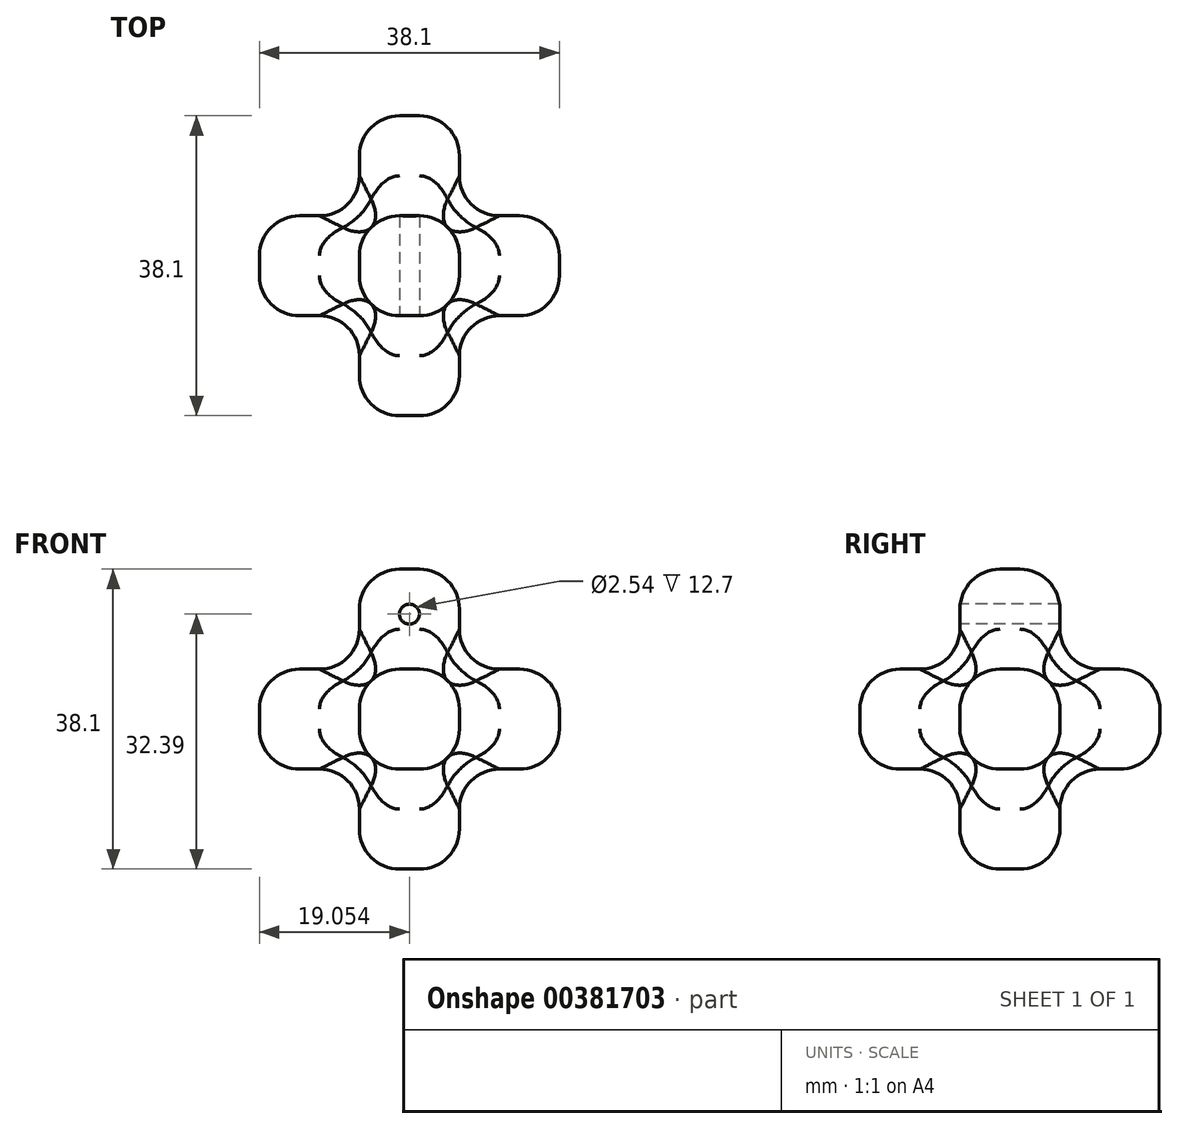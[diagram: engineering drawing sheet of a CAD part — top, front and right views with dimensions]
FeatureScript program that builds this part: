
annotation { "Feature Type Name" : "Feature", "Feature Type Description" : "" }
export const myFeature = defineFeature(function(context is Context, id is Id, definition is map)
    precondition{}
    {
        {
            var Q0;
            Q0=qCreatedBy(makeId("Front.planeOp"),FACE);
            var sketch = newSketch(context, id + "F0", { "sketchPlane" : qUnion([Q0])});
            skLineSegment(sketch, "E0", {"start": v(-30.28, 47.13) * mm, "end": v(-30.28, 34.43) * mm});
            skLineSegment(sketch, "E1", {"start": v(-30.28, 34.43) * mm, "end": v(-17.58, 34.43) * mm});
            skLineSegment(sketch, "E2", {"start": v(-17.58, 34.43) * mm, "end": v(-17.58, 21.73) * mm});
            skLineSegment(sketch, "E3", {"start": v(-17.58, 21.73) * mm, "end": v(-30.28, 21.73) * mm});
            skLineSegment(sketch, "E4", {"start": v(-30.28, 21.73) * mm, "end": v(-30.28, 9.03) * mm});
            skLineSegment(sketch, "E5", {"start": v(-30.28, 9.03) * mm, "end": v(-42.98, 9.03) * mm});
            skLineSegment(sketch, "E6", {"start": v(-42.98, 9.03) * mm, "end": v(-42.98, 21.73) * mm});
            skLineSegment(sketch, "E7", {"start": v(-42.98, 21.73) * mm, "end": v(-55.68, 21.73) * mm});
            skLineSegment(sketch, "E8", {"start": v(-55.68, 21.73) * mm, "end": v(-55.68, 34.43) * mm});
            skLineSegment(sketch, "E9", {"start": v(-55.68, 34.43) * mm, "end": v(-42.98, 34.43) * mm});
            skLineSegment(sketch, "E10", {"start": v(-42.98, 34.43) * mm, "end": v(-42.98, 47.13) * mm});
            skLineSegment(sketch, "E11", {"start": v(-42.98, 47.13) * mm, "end": v(-30.28, 47.13) * mm});
            skSolve(sketch);
        }
        {
            var Q0;
            Q0=makeQuery(id+"F0.imprint","IMPRINT",FACE,{"disambiguationData":[TD([[makeQuery(id+"F0.imprint","IMPRINT",EDGE,{"derivedFrom":sQuery(id+"F0.wireOp",EDGE,"E0")}),-1.0]])]});
            extrude(context, id + "F1", {"entities" : qUnion([Q0]), "depth" : 12.7 * mm});
        }
        {
            var Q0;
            Q0=makeQuery(id+"F1.opExtrude","CAP_FACE",FACE,{"disambiguationData":[OSD([sQuery(id+"F0.wireOp",EDGE,"E0"),sQuery(id+"F0.wireOp",EDGE,"E1"),sQuery(id+"F0.wireOp",EDGE,"E2"),sQuery(id+"F0.wireOp",EDGE,"E3"),sQuery(id+"F0.wireOp",EDGE,"E4"),sQuery(id+"F0.wireOp",EDGE,"E5"),sQuery(id+"F0.wireOp",EDGE,"E6"),sQuery(id+"F0.wireOp",EDGE,"E7"),sQuery(id+"F0.wireOp",EDGE,"E8"),sQuery(id+"F0.wireOp",EDGE,"E9"),sQuery(id+"F0.wireOp",EDGE,"E10"),sQuery(id+"F0.wireOp",EDGE,"E11")])],"isStart":false});
            var sketch = newSketch(context, id + "F2", { "sketchPlane" : qUnion([Q0])});
            skLineSegment(sketch, "E12", {"start": v(-42.98, 34.43) * mm, "end": v(-30.28, 34.43) * mm});
            skLineSegment(sketch, "E13", {"start": v(-30.28, 34.43) * mm, "end": v(-30.28, 21.73) * mm});
            skLineSegment(sketch, "E14", {"start": v(-30.28, 21.73) * mm, "end": v(-42.98, 21.73) * mm});
            skLineSegment(sketch, "E15", {"start": v(-42.98, 21.73) * mm, "end": v(-42.98, 34.43) * mm});
            skSolve(sketch);
        }
        {
            var Q0;
            Q0=makeQuery(id+"F2.imprint","IMPRINT",FACE,{"disambiguationData":[TD([[makeQuery(id+"F2.imprint","IMPRINT",EDGE,{"derivedFrom":sQuery(id+"F2.wireOp",EDGE,"E12")}),-1.0]])]});
            extrude(context, id + "F3", {"entities" : qUnion([Q0]), "operationType" : NewBodyOperationType.ADD, "depth" : 12.7 * mm});
        }
        {
            var Q0;
            Q0=makeQuery(id+"F1.opExtrude","CAP_FACE",FACE,{"disambiguationData":[OSD([sQuery(id+"F0.wireOp",EDGE,"E0"),sQuery(id+"F0.wireOp",EDGE,"E1"),sQuery(id+"F0.wireOp",EDGE,"E2"),sQuery(id+"F0.wireOp",EDGE,"E3"),sQuery(id+"F0.wireOp",EDGE,"E4"),sQuery(id+"F0.wireOp",EDGE,"E5"),sQuery(id+"F0.wireOp",EDGE,"E6"),sQuery(id+"F0.wireOp",EDGE,"E7"),sQuery(id+"F0.wireOp",EDGE,"E8"),sQuery(id+"F0.wireOp",EDGE,"E9"),sQuery(id+"F0.wireOp",EDGE,"E10"),sQuery(id+"F0.wireOp",EDGE,"E11")])],"isStart":true});
            var sketch = newSketch(context, id + "F4", { "sketchPlane" : qUnion([Q0])});
            skLineSegment(sketch, "E16", {"start": v(30.28, 34.43) * mm, "end": v(42.98, 34.43) * mm});
            skLineSegment(sketch, "E17", {"start": v(42.98, 34.43) * mm, "end": v(42.98, 21.73) * mm});
            skLineSegment(sketch, "E18", {"start": v(42.98, 21.73) * mm, "end": v(30.28, 21.73) * mm});
            skLineSegment(sketch, "E19", {"start": v(30.28, 21.73) * mm, "end": v(30.28, 34.43) * mm});
            skSolve(sketch);
        }
        {
            var Q0;
            Q0=qSketchRegion(id+"F4",true);
            extrude(context, id + "F5", {"entities" : qUnion([Q0]), "operationType" : NewBodyOperationType.ADD, "depth" : 12.7 * mm});
        }
        {
            var Q0;
            Q0=makeQuery(id+"F1.opExtrude","SWEPT_EDGE",EDGE,{"disambiguationData":[OSD([sQuery(id+"F0.wireOp",EDGE,"E10"),sQuery(id+"F0.wireOp",EDGE,"E11")])]});
            var Q1;
            Q1=makeQuery(id+"F1.opExtrude","CAP_EDGE",EDGE,{"disambiguationData":[OSD([sQuery(id+"F0.wireOp",EDGE,"E11")])],"isStart":false});
            var Q2;
            Q2=makeQuery(id+"F1.opExtrude","CAP_EDGE",EDGE,{"disambiguationData":[OSD([sQuery(id+"F0.wireOp",EDGE,"E11")])],"isStart":true});
            var Q3;
            Q3=makeQuery(id+"F1.opExtrude","SWEPT_EDGE",EDGE,{"disambiguationData":[OSD([sQuery(id+"F0.wireOp",EDGE,"E0"),sQuery(id+"F0.wireOp",EDGE,"E11")])]});
            var Q4;
            Q4=makeQuery(id+"F1.opExtrude","CAP_EDGE",EDGE,{"disambiguationData":[OSD([sQuery(id+"F0.wireOp",EDGE,"E10")])],"isStart":false});
            var Q5;
            Q5=makeQuery(id+"F1.opExtrude","CAP_EDGE",EDGE,{"disambiguationData":[OSD([sQuery(id+"F0.wireOp",EDGE,"E0")])],"isStart":false});
            var Q6;
            Q6=makeQuery(id+"F1.opExtrude","CAP_EDGE",EDGE,{"disambiguationData":[OSD([sQuery(id+"F0.wireOp",EDGE,"E0")])],"isStart":true});
            var Q7;
            Q7=makeQuery(id+"F1.opExtrude","CAP_EDGE",EDGE,{"disambiguationData":[OSD([sQuery(id+"F0.wireOp",EDGE,"E10")])],"isStart":true});
            fillet(context, id + "F6", {"entities" : qUnion([Q0, Q1, Q2, Q3, Q4, Q5, Q6, Q7]), "radius" : 5.08 * mm, "tangentPropagation" : true, "allowEdgeOverflow" : false});
        }
        {
            var Q0;
            Q0=makeQuery(id+"F3.opExtrude","SWEPT_EDGE",EDGE,{"disambiguationData":[OSD([sQuery(id+"F0.wireOp",EDGE,"E9"),sQuery(id+"F0.wireOp",EDGE,"E10"),sQuery(id+"F2.wireOp",EDGE,"E12"),sQuery(id+"F2.wireOp",EDGE,"E15")])]});
            var Q1;
            Q1=makeQuery(id+"F3.opExtrude","SWEPT_EDGE",EDGE,{"disambiguationData":[OSD([sQuery(id+"F0.wireOp",EDGE,"E0"),sQuery(id+"F0.wireOp",EDGE,"E1"),sQuery(id+"F2.wireOp",EDGE,"E12"),sQuery(id+"F2.wireOp",EDGE,"E13")])]});
            var Q2;
            Q2=makeQuery(id+"F3.opExtrude","SWEPT_EDGE",EDGE,{"disambiguationData":[OSD([sQuery(id+"F0.wireOp",EDGE,"E6"),sQuery(id+"F0.wireOp",EDGE,"E7"),sQuery(id+"F2.wireOp",EDGE,"E14"),sQuery(id+"F2.wireOp",EDGE,"E15")])]});
            var Q3;
            Q3=makeQuery(id+"F3.opExtrude","SWEPT_EDGE",EDGE,{"disambiguationData":[OSD([sQuery(id+"F0.wireOp",EDGE,"E3"),sQuery(id+"F0.wireOp",EDGE,"E4"),sQuery(id+"F2.wireOp",EDGE,"E13"),sQuery(id+"F2.wireOp",EDGE,"E14")])]});
            var Q4;
            Q4=makeQuery(id+"F3.opExtrude","CAP_EDGE",EDGE,{"disambiguationData":[OSD([sQuery(id+"F2.wireOp",EDGE,"E15")])],"isStart":false});
            var Q5;
            Q5=makeQuery(id+"F3.opExtrude","CAP_EDGE",EDGE,{"disambiguationData":[OSD([sQuery(id+"F2.wireOp",EDGE,"E12")])],"isStart":false});
            var Q6;
            Q6=makeQuery(id+"F3.opExtrude","CAP_EDGE",EDGE,{"disambiguationData":[OSD([sQuery(id+"F2.wireOp",EDGE,"E13")])],"isStart":false});
            var Q7;
            Q7=makeQuery(id+"F3.opExtrude","CAP_EDGE",EDGE,{"disambiguationData":[OSD([sQuery(id+"F2.wireOp",EDGE,"E14")])],"isStart":false});
            fillet(context, id + "F7", {"entities" : qUnion([Q0, Q1, Q2, Q3, Q4, Q5, Q6, Q7]), "radius" : 5.08 * mm, "tangentPropagation" : true, "allowEdgeOverflow" : false});
        }
        {
            var Q0;
            Q0=makeQuery(id+"F1.opExtrude","SWEPT_FACE",FACE,{"disambiguationData":[OSD([sQuery(id+"F0.wireOp",EDGE,"E8")])]});
            var Q1;
            Q1=makeQuery(id+"F1.opExtrude","CAP_EDGE",EDGE,{"disambiguationData":[OSD([sQuery(id+"F0.wireOp",EDGE,"E8")])],"isStart":false});
            var Q2;
            Q2=makeQuery(id+"F1.opExtrude","CAP_EDGE",EDGE,{"disambiguationData":[OSD([sQuery(id+"F0.wireOp",EDGE,"E8")])],"isStart":true});
            var Q3;
            Q3=makeQuery(id+"F1.opExtrude","CAP_EDGE",EDGE,{"disambiguationData":[OSD([sQuery(id+"F0.wireOp",EDGE,"E9")])],"isStart":true});
            var Q4;
            Q4=makeQuery(id+"F1.opExtrude","CAP_EDGE",EDGE,{"disambiguationData":[OSD([sQuery(id+"F0.wireOp",EDGE,"E7")])],"isStart":false});
            var Q5;
            Q5=makeQuery(id+"F1.opExtrude","CAP_EDGE",EDGE,{"disambiguationData":[OSD([sQuery(id+"F0.wireOp",EDGE,"E7")])],"isStart":true});
            var Q6;
            Q6=makeQuery(id+"F1.opExtrude","CAP_EDGE",EDGE,{"disambiguationData":[OSD([sQuery(id+"F0.wireOp",EDGE,"E9")])],"isStart":false});
            fillet(context, id + "F8", {"entities" : qUnion([Q0, Q1, Q2, Q3, Q4, Q5, Q6]), "radius" : 5.08 * mm, "tangentPropagation" : true, "allowEdgeOverflow" : false});
        }
        {
            var Q0;
            Q0=makeQuery(id+"F1.opExtrude","CAP_EDGE",EDGE,{"disambiguationData":[OSD([sQuery(id+"F0.wireOp",EDGE,"E1")])],"isStart":false});
            var Q1;
            Q1=makeQuery(id+"F1.opExtrude","CAP_EDGE",EDGE,{"disambiguationData":[OSD([sQuery(id+"F0.wireOp",EDGE,"E1")])],"isStart":true});
            var Q2;
            Q2=makeQuery(id+"F1.opExtrude","SWEPT_EDGE",EDGE,{"disambiguationData":[OSD([sQuery(id+"F0.wireOp",EDGE,"E1"),sQuery(id+"F0.wireOp",EDGE,"E2")])]});
            var Q3;
            Q3=makeQuery(id+"F1.opExtrude","CAP_EDGE",EDGE,{"disambiguationData":[OSD([sQuery(id+"F0.wireOp",EDGE,"E2")])],"isStart":true});
            var Q4;
            Q4=makeQuery(id+"F1.opExtrude","SWEPT_EDGE",EDGE,{"disambiguationData":[OSD([sQuery(id+"F0.wireOp",EDGE,"E2"),sQuery(id+"F0.wireOp",EDGE,"E3")])]});
            var Q5;
            Q5=makeQuery(id+"F1.opExtrude","CAP_EDGE",EDGE,{"disambiguationData":[OSD([sQuery(id+"F0.wireOp",EDGE,"E2")])],"isStart":false});
            var Q6;
            Q6=makeQuery(id+"F1.opExtrude","CAP_EDGE",EDGE,{"disambiguationData":[OSD([sQuery(id+"F0.wireOp",EDGE,"E3")])],"isStart":false});
            var Q7;
            Q7=makeQuery(id+"F1.opExtrude","CAP_EDGE",EDGE,{"disambiguationData":[OSD([sQuery(id+"F0.wireOp",EDGE,"E3")])],"isStart":true});
            fillet(context, id + "F9", {"entities" : qUnion([Q0, Q1, Q2, Q3, Q4, Q5, Q6, Q7]), "radius" : 5.08 * mm, "tangentPropagation" : true, "allowEdgeOverflow" : false});
        }
        {
            var Q0;
            Q0=makeQuery(id+"F1.opExtrude","CAP_EDGE",EDGE,{"disambiguationData":[OSD([sQuery(id+"F0.wireOp",EDGE,"E6")])],"isStart":true});
            var Q1;
            Q1=makeQuery(id+"F1.opExtrude","CAP_EDGE",EDGE,{"disambiguationData":[OSD([sQuery(id+"F0.wireOp",EDGE,"E6")])],"isStart":false});
            var Q2;
            Q2=makeQuery(id+"F1.opExtrude","CAP_EDGE",EDGE,{"disambiguationData":[OSD([sQuery(id+"F0.wireOp",EDGE,"E4")])],"isStart":false});
            var Q3;
            Q3=makeQuery(id+"F1.opExtrude","CAP_EDGE",EDGE,{"disambiguationData":[OSD([sQuery(id+"F0.wireOp",EDGE,"E4")])],"isStart":true});
            var Q4;
            Q4=makeQuery(id+"F1.opExtrude","SWEPT_EDGE",EDGE,{"disambiguationData":[OSD([sQuery(id+"F0.wireOp",EDGE,"E4"),sQuery(id+"F0.wireOp",EDGE,"E5")])]});
            var Q5;
            Q5=makeQuery(id+"F1.opExtrude","CAP_EDGE",EDGE,{"disambiguationData":[OSD([sQuery(id+"F0.wireOp",EDGE,"E5")])],"isStart":false});
            var Q6;
            Q6=makeQuery(id+"F1.opExtrude","SWEPT_EDGE",EDGE,{"disambiguationData":[OSD([sQuery(id+"F0.wireOp",EDGE,"E5"),sQuery(id+"F0.wireOp",EDGE,"E6")])]});
            var Q7;
            Q7=makeQuery(id+"F1.opExtrude","CAP_EDGE",EDGE,{"disambiguationData":[OSD([sQuery(id+"F0.wireOp",EDGE,"E5")])],"isStart":true});
            fillet(context, id + "F10", {"entities" : qUnion([Q0, Q1, Q2, Q3, Q4, Q5, Q6, Q7]), "radius" : 5.08 * mm, "tangentPropagation" : true, "allowEdgeOverflow" : false});
        }
        {
            var Q0;
            Q0=makeQuery(id+"F5.opExtrude","SWEPT_EDGE",EDGE,{"disambiguationData":[OSD([sQuery(id+"F0.wireOp",EDGE,"E3"),sQuery(id+"F0.wireOp",EDGE,"E4"),sQuery(id+"F4.wireOp",EDGE,"E18"),sQuery(id+"F4.wireOp",EDGE,"E19")])]});
            fillet(context, id + "F11", {"entities" : qUnion([Q0]), "radius" : 5.08 * mm, "tangentPropagation" : true, "allowEdgeOverflow" : false});
        }
        {
            var Q0;
            Q0=makeQuery(id+"F5.opExtrude","SWEPT_EDGE",EDGE,{"disambiguationData":[OSD([sQuery(id+"F0.wireOp",EDGE,"E0"),sQuery(id+"F0.wireOp",EDGE,"E1"),sQuery(id+"F4.wireOp",EDGE,"E16"),sQuery(id+"F4.wireOp",EDGE,"E19")])]});
            var Q1;
            Q1=makeQuery(id+"F5.opExtrude","SWEPT_EDGE",EDGE,{"disambiguationData":[OSD([sQuery(id+"F0.wireOp",EDGE,"E9"),sQuery(id+"F0.wireOp",EDGE,"E10"),sQuery(id+"F4.wireOp",EDGE,"E16"),sQuery(id+"F4.wireOp",EDGE,"E17")])]});
            var Q2;
            Q2=makeQuery(id+"F5.opExtrude","SWEPT_EDGE",EDGE,{"disambiguationData":[OSD([sQuery(id+"F0.wireOp",EDGE,"E6"),sQuery(id+"F0.wireOp",EDGE,"E7"),sQuery(id+"F4.wireOp",EDGE,"E17"),sQuery(id+"F4.wireOp",EDGE,"E18")])]});
            fillet(context, id + "F12", {"entities" : qUnion([Q0, Q1, Q2]), "radius" : 5.08 * mm, "tangentPropagation" : true, "allowEdgeOverflow" : false});
        }
        {
            var Q0;
            Q0=makeQuery(id+"F5.opExtrude","CAP_FACE",FACE,{"disambiguationData":[OSD([sQuery(id+"F4.wireOp",EDGE,"E16"),sQuery(id+"F4.wireOp",EDGE,"E17"),sQuery(id+"F4.wireOp",EDGE,"E18"),sQuery(id+"F4.wireOp",EDGE,"E19")])],"isStart":false});
            var Q1;
            {var subQ0=sQuery(id+"F0.wireOp",EDGE,"E9");var subQ1=makeQuery(id+"F1.opExtrude","SWEPT_FACE",FACE,{"disambiguationData":[OSD([subQ0])]});var subQ2=sQuery(id+"F0.wireOp",EDGE,"E0");var subQ4=sQuery(id+"F0.wireOp",EDGE,"E1");var subQ5=makeQuery(id+"F1.opExtrude","SWEPT_FACE",FACE,{"disambiguationData":[OSD([subQ4])]});var subQ6=sQuery(id+"F0.wireOp",EDGE,"E11");var subQ7=sQuery(id+"F0.wireOp",EDGE,"E10");var subQ8=sQuery(id+"F0.wireOp",EDGE,"E8");var subQ9=sQuery(id+"F0.wireOp",EDGE,"E7");var subQ10=sQuery(id+"F0.wireOp",EDGE,"E6");var subQ11=sQuery(id+"F0.wireOp",EDGE,"E5");var subQ12=sQuery(id+"F0.wireOp",EDGE,"E4");var subQ13=sQuery(id+"F0.wireOp",EDGE,"E3");var subQ14=sQuery(id+"F0.wireOp",EDGE,"E2");var subQ15=makeQuery(id+"F1.opExtrude","CAP_FACE",FACE,{"disambiguationData":[OSD([subQ2,subQ4,subQ14,subQ13,subQ12,subQ11,subQ10,subQ9,subQ8,subQ0,subQ7,subQ6])],"isStart":false});var subQ17=sQuery(id+"F2.wireOp",EDGE,"E12");var subQ18=makeQuery(id+"F3.opExtrude","SWEPT_FACE",FACE,{"disambiguationData":[OSD([subQ17])]});var subQ19=sQuery(id+"F2.wireOp",EDGE,"E13");Q1=makeQuery(id+"F9.opFillet","TWEAK_EDGE",EDGE,{"derivedFrom":[makeQuery(id+"F7.opFillet","BLEND_VERTEX",VERTEX,{"blendedFrom":[makeQuery(id+"F3.opExtrude","SWEPT_EDGE",EDGE,{"disambiguationData":[OSD([subQ2,subQ4,subQ17,subQ19])]}),makeQuery(id+"F3.boolean.opBoolean","SPLIT",FACE,{"disambiguationData":[TD([makeQuery(id+"F1.opExtrude","SWEPT_FACE",FACE,{"disambiguationData":[OSD([subQ14])]})])],"derivedFrom":subQ15}),makeQuery(id+"F3.boolean.opBoolean","SPLIT",FACE,{"disambiguationData":[TD([makeQuery(id+"F1.opExtrude","SWEPT_FACE",FACE,{"disambiguationData":[OSD([subQ11])]})])],"derivedFrom":subQ15}),makeQuery(id+"F3.boolean.opBoolean","SPLIT",FACE,{"disambiguationData":[TD([makeQuery(id+"F1.opExtrude","SWEPT_FACE",FACE,{"disambiguationData":[OSD([subQ8])]})])],"derivedFrom":subQ15}),makeQuery(id+"F6.opFillet","BLEND_FACE",FACE,{"disambiguationData":[OSD([subQ2]),TDD([makeQuery(id+"F1.opExtrude","CAP_EDGE",EDGE,{"disambiguationData":[OSD([subQ2])],"isStart":false})])]}),makeQuery(id+"F6.opFillet","MERGE",FACE,{"derivedFrom":[subQ5,subQ1,subQ18,makeQuery(id+"F5.opExtrude","SWEPT_FACE",FACE,{"disambiguationData":[OSD([sQuery(id+"F4.wireOp",EDGE,"E16")])]})]}),makeQuery(id+"F3.boolean.opBoolean","SPLIT",FACE,{"disambiguationData":[TD([makeQuery(id+"F1.opExtrude","SWEPT_FACE",FACE,{"disambiguationData":[OSD([subQ6])]})])],"derivedFrom":subQ15})],"blendedInto":[makeQuery(id+"F3.boolean.opBoolean","SPLIT",FACE,{"disambiguationData":[TD([makeQuery(id+"F1.opExtrude","SWEPT_FACE",FACE,{"disambiguationData":[OSD([subQ14])]})])],"derivedFrom":subQ15}),makeQuery(id+"F3.boolean.opBoolean","SPLIT",FACE,{"disambiguationData":[TD([makeQuery(id+"F1.opExtrude","SWEPT_FACE",FACE,{"disambiguationData":[OSD([subQ11])]})])],"derivedFrom":subQ15}),makeQuery(id+"F3.boolean.opBoolean","SPLIT",FACE,{"disambiguationData":[TD([makeQuery(id+"F1.opExtrude","SWEPT_FACE",FACE,{"disambiguationData":[OSD([subQ8])]})])],"derivedFrom":subQ15}),makeQuery(id+"F6.opFillet","BLEND_FACE",FACE,{"disambiguationData":[OSD([subQ2]),TDD([makeQuery(id+"F1.opExtrude","CAP_EDGE",EDGE,{"disambiguationData":[OSD([subQ2])],"isStart":false})])]}),makeQuery(id+"F6.opFillet","MERGE",FACE,{"derivedFrom":[subQ5,subQ1,subQ18,makeQuery(id+"F5.opExtrude","SWEPT_FACE",FACE,{"disambiguationData":[OSD([sQuery(id+"F4.wireOp",EDGE,"E16")])]})]}),makeQuery(id+"F3.boolean.opBoolean","SPLIT",FACE,{"disambiguationData":[TD([makeQuery(id+"F1.opExtrude","SWEPT_FACE",FACE,{"disambiguationData":[OSD([subQ6])]})])],"derivedFrom":subQ15})]})]});}
            var Q2;
            {var subQ0=sQuery(id+"F0.wireOp",EDGE,"E10");Q2=makeQuery(id+"F8.opFillet","BLEND_EDGE",EDGE,{"blendedFrom":[makeQuery(id+"F1.opExtrude","CAP_EDGE",EDGE,{"disambiguationData":[OSD([sQuery(id+"F0.wireOp",EDGE,"E9")])],"isStart":false}),makeQuery(id+"F6.opFillet","BLEND_FACE",FACE,{"disambiguationData":[OSD([subQ0]),TDD([makeQuery(id+"F1.opExtrude","CAP_EDGE",EDGE,{"disambiguationData":[OSD([subQ0])],"isStart":false})])]})],"blendedInto":[makeQuery(id+"F6.opFillet","BLEND_FACE",FACE,{"disambiguationData":[OSD([subQ0]),TDD([makeQuery(id+"F1.opExtrude","CAP_EDGE",EDGE,{"disambiguationData":[OSD([subQ0])],"isStart":false})])]})]});}
            var Q3;
            {var subQ0=sQuery(id+"F0.wireOp",EDGE,"E9");var subQ1=makeQuery(id+"F1.opExtrude","SWEPT_FACE",FACE,{"disambiguationData":[OSD([subQ0])]});var subQ2=sQuery(id+"F0.wireOp",EDGE,"E0");var subQ4=sQuery(id+"F0.wireOp",EDGE,"E1");var subQ5=makeQuery(id+"F1.opExtrude","SWEPT_FACE",FACE,{"disambiguationData":[OSD([subQ4])]});var subQ6=sQuery(id+"F0.wireOp",EDGE,"E11");var subQ7=sQuery(id+"F0.wireOp",EDGE,"E10");var subQ8=sQuery(id+"F0.wireOp",EDGE,"E8");var subQ9=sQuery(id+"F0.wireOp",EDGE,"E7");var subQ10=sQuery(id+"F0.wireOp",EDGE,"E6");var subQ11=sQuery(id+"F0.wireOp",EDGE,"E5");var subQ12=sQuery(id+"F0.wireOp",EDGE,"E4");var subQ13=sQuery(id+"F0.wireOp",EDGE,"E3");var subQ14=sQuery(id+"F0.wireOp",EDGE,"E2");var subQ15=makeQuery(id+"F1.opExtrude","CAP_FACE",FACE,{"disambiguationData":[OSD([subQ2,subQ4,subQ14,subQ13,subQ12,subQ11,subQ10,subQ9,subQ8,subQ0,subQ7,subQ6])],"isStart":false});var subQ17=sQuery(id+"F2.wireOp",EDGE,"E12");var subQ18=makeQuery(id+"F3.opExtrude","SWEPT_FACE",FACE,{"disambiguationData":[OSD([subQ17])]});var subQ20=sQuery(id+"F2.wireOp",EDGE,"E15");Q3=makeQuery(id+"F8.opFillet","TWEAK_EDGE",EDGE,{"derivedFrom":[makeQuery(id+"F7.opFillet","BLEND_VERTEX",VERTEX,{"blendedFrom":[makeQuery(id+"F3.opExtrude","SWEPT_EDGE",EDGE,{"disambiguationData":[OSD([subQ0,subQ7,subQ17,subQ20])]}),makeQuery(id+"F3.boolean.opBoolean","SPLIT",FACE,{"disambiguationData":[TD([makeQuery(id+"F1.opExtrude","SWEPT_FACE",FACE,{"disambiguationData":[OSD([subQ14])]})])],"derivedFrom":subQ15}),makeQuery(id+"F3.boolean.opBoolean","SPLIT",FACE,{"disambiguationData":[TD([makeQuery(id+"F1.opExtrude","SWEPT_FACE",FACE,{"disambiguationData":[OSD([subQ11])]})])],"derivedFrom":subQ15}),makeQuery(id+"F3.boolean.opBoolean","SPLIT",FACE,{"disambiguationData":[TD([makeQuery(id+"F1.opExtrude","SWEPT_FACE",FACE,{"disambiguationData":[OSD([subQ8])]})])],"derivedFrom":subQ15}),makeQuery(id+"F6.opFillet","BLEND_FACE",FACE,{"disambiguationData":[OSD([subQ7]),TDD([makeQuery(id+"F1.opExtrude","CAP_EDGE",EDGE,{"disambiguationData":[OSD([subQ7])],"isStart":false})])]}),makeQuery(id+"F6.opFillet","MERGE",FACE,{"derivedFrom":[subQ5,subQ1,subQ18,makeQuery(id+"F5.opExtrude","SWEPT_FACE",FACE,{"disambiguationData":[OSD([sQuery(id+"F4.wireOp",EDGE,"E16")])]})]}),makeQuery(id+"F3.boolean.opBoolean","SPLIT",FACE,{"disambiguationData":[TD([makeQuery(id+"F1.opExtrude","SWEPT_FACE",FACE,{"disambiguationData":[OSD([subQ6])]})])],"derivedFrom":subQ15})],"blendedInto":[makeQuery(id+"F3.boolean.opBoolean","SPLIT",FACE,{"disambiguationData":[TD([makeQuery(id+"F1.opExtrude","SWEPT_FACE",FACE,{"disambiguationData":[OSD([subQ14])]})])],"derivedFrom":subQ15}),makeQuery(id+"F3.boolean.opBoolean","SPLIT",FACE,{"disambiguationData":[TD([makeQuery(id+"F1.opExtrude","SWEPT_FACE",FACE,{"disambiguationData":[OSD([subQ11])]})])],"derivedFrom":subQ15}),makeQuery(id+"F3.boolean.opBoolean","SPLIT",FACE,{"disambiguationData":[TD([makeQuery(id+"F1.opExtrude","SWEPT_FACE",FACE,{"disambiguationData":[OSD([subQ8])]})])],"derivedFrom":subQ15}),makeQuery(id+"F6.opFillet","BLEND_FACE",FACE,{"disambiguationData":[OSD([subQ7]),TDD([makeQuery(id+"F1.opExtrude","CAP_EDGE",EDGE,{"disambiguationData":[OSD([subQ7])],"isStart":false})])]}),makeQuery(id+"F6.opFillet","MERGE",FACE,{"derivedFrom":[subQ5,subQ1,subQ18,makeQuery(id+"F5.opExtrude","SWEPT_FACE",FACE,{"disambiguationData":[OSD([sQuery(id+"F4.wireOp",EDGE,"E16")])]})]}),makeQuery(id+"F3.boolean.opBoolean","SPLIT",FACE,{"disambiguationData":[TD([makeQuery(id+"F1.opExtrude","SWEPT_FACE",FACE,{"disambiguationData":[OSD([subQ6])]})])],"derivedFrom":subQ15})]})]});}
            var Q4;
            {var subQ0=sQuery(id+"F2.wireOp",EDGE,"E15");var subQ1=sQuery(id+"F2.wireOp",EDGE,"E12");var subQ2=sQuery(id+"F0.wireOp",EDGE,"E10");var subQ3=sQuery(id+"F0.wireOp",EDGE,"E9");Q4=makeQuery(id+"F8.opFillet","BLEND_EDGE",EDGE,{"blendedFrom":[makeQuery(id+"F1.opExtrude","CAP_EDGE",EDGE,{"disambiguationData":[OSD([subQ3])],"isStart":false}),makeQuery(id+"F7.opFillet","BLEND_FACE",FACE,{"disambiguationData":[OSD([subQ3,subQ2,subQ1,subQ0]),TDD([makeQuery(id+"F3.opExtrude","SWEPT_EDGE",EDGE,{"disambiguationData":[OSD([subQ3,subQ2,subQ1,subQ0])]})])]})],"blendedInto":[makeQuery(id+"F7.opFillet","BLEND_FACE",FACE,{"disambiguationData":[OSD([subQ3,subQ2,subQ1,subQ0]),TDD([makeQuery(id+"F3.opExtrude","SWEPT_EDGE",EDGE,{"disambiguationData":[OSD([subQ3,subQ2,subQ1,subQ0])]})])]})]});}
            var Q5;
            Q5=makeQuery(id+"F3.opExtrude","CAP_EDGE",EDGE,{"disambiguationData":[OSD([sQuery(id+"F2.wireOp",EDGE,"E12")])],"isStart":true});
            var Q6;
            {var subQ0=sQuery(id+"F0.wireOp",EDGE,"E7");Q6=makeQuery(id+"F10.opFillet","BLEND_EDGE",EDGE,{"blendedFrom":[makeQuery(id+"F1.opExtrude","CAP_EDGE",EDGE,{"disambiguationData":[OSD([sQuery(id+"F0.wireOp",EDGE,"E6")])],"isStart":false}),makeQuery(id+"F8.opFillet","BLEND_FACE",FACE,{"disambiguationData":[OSD([subQ0]),TDD([makeQuery(id+"F1.opExtrude","CAP_EDGE",EDGE,{"disambiguationData":[OSD([subQ0])],"isStart":false})])]})],"blendedInto":[makeQuery(id+"F8.opFillet","BLEND_FACE",FACE,{"disambiguationData":[OSD([subQ0]),TDD([makeQuery(id+"F1.opExtrude","CAP_EDGE",EDGE,{"disambiguationData":[OSD([subQ0])],"isStart":false})])]})]});}
            var Q7;
            {var subQ0=sQuery(id+"F2.wireOp",EDGE,"E15");var subQ1=sQuery(id+"F2.wireOp",EDGE,"E14");var subQ2=sQuery(id+"F0.wireOp",EDGE,"E7");var subQ3=sQuery(id+"F0.wireOp",EDGE,"E6");Q7=makeQuery(id+"F10.opFillet","BLEND_EDGE",EDGE,{"blendedFrom":[makeQuery(id+"F1.opExtrude","CAP_EDGE",EDGE,{"disambiguationData":[OSD([subQ3])],"isStart":false}),makeQuery(id+"F7.opFillet","BLEND_FACE",FACE,{"disambiguationData":[OSD([subQ3,subQ2,subQ1,subQ0]),TDD([makeQuery(id+"F3.opExtrude","SWEPT_EDGE",EDGE,{"disambiguationData":[OSD([subQ3,subQ2,subQ1,subQ0])]})])]})],"blendedInto":[makeQuery(id+"F7.opFillet","BLEND_FACE",FACE,{"disambiguationData":[OSD([subQ3,subQ2,subQ1,subQ0]),TDD([makeQuery(id+"F3.opExtrude","SWEPT_EDGE",EDGE,{"disambiguationData":[OSD([subQ3,subQ2,subQ1,subQ0])]})])]})]});}
            var Q8;
            {var subQ0=sQuery(id+"F2.wireOp",EDGE,"E15");var subQ1=makeQuery(id+"F3.opExtrude","SWEPT_FACE",FACE,{"disambiguationData":[OSD([subQ0])]});var subQ2=sQuery(id+"F0.wireOp",EDGE,"E8");var subQ3=sQuery(id+"F0.wireOp",EDGE,"E7");var subQ5=sQuery(id+"F0.wireOp",EDGE,"E6");var subQ6=makeQuery(id+"F1.opExtrude","SWEPT_FACE",FACE,{"disambiguationData":[OSD([subQ5])]});var subQ7=sQuery(id+"F0.wireOp",EDGE,"E10");var subQ8=sQuery(id+"F0.wireOp",EDGE,"E9");var subQ9=sQuery(id+"F0.wireOp",EDGE,"E5");var subQ10=sQuery(id+"F0.wireOp",EDGE,"E4");var subQ11=sQuery(id+"F0.wireOp",EDGE,"E3");var subQ12=sQuery(id+"F0.wireOp",EDGE,"E2");var subQ13=sQuery(id+"F0.wireOp",EDGE,"E1");var subQ14=sQuery(id+"F0.wireOp",EDGE,"E0");var subQ15=makeQuery(id+"F1.opExtrude","CAP_FACE",FACE,{"disambiguationData":[OSD([subQ14,subQ13,subQ12,subQ11,subQ10,subQ9,subQ5,subQ3,subQ2,subQ8,subQ7,sQuery(id+"F0.wireOp",EDGE,"E11")])],"isStart":false});var subQ17=sQuery(id+"F2.wireOp",EDGE,"E14");Q8=makeQuery(id+"F10.opFillet","TWEAK_EDGE",EDGE,{"derivedFrom":[makeQuery(id+"F8.opFillet","BLEND_VERTEX",VERTEX,{"blendedFrom":[makeQuery(id+"F1.opExtrude","CAP_EDGE",EDGE,{"disambiguationData":[OSD([subQ3])],"isStart":false}),subQ6,makeQuery(id+"F5.opExtrude","SWEPT_FACE",FACE,{"disambiguationData":[OSD([sQuery(id+"F4.wireOp",EDGE,"E17")])]}),makeQuery(id+"F7.opFillet","BLEND_FACE",FACE,{"disambiguationData":[OSD([subQ5,subQ3,subQ17,subQ0]),TDD([makeQuery(id+"F3.opExtrude","SWEPT_EDGE",EDGE,{"disambiguationData":[OSD([subQ5,subQ3,subQ17,subQ0])]})])]}),makeQuery(id+"F7.opFillet","MERGE",FACE,{"derivedFrom":[makeQuery(id+"F3.boolean.opBoolean","SPLIT",FACE,{"disambiguationData":[TD([makeQuery(id+"F1.opExtrude","SWEPT_FACE",FACE,{"disambiguationData":[OSD([subQ12])]})])],"derivedFrom":subQ15}),makeQuery(id+"F3.boolean.opBoolean","SPLIT",FACE,{"disambiguationData":[TD([makeQuery(id+"F1.opExtrude","SWEPT_FACE",FACE,{"disambiguationData":[OSD([subQ9])]})])],"derivedFrom":subQ15}),makeQuery(id+"F3.boolean.opBoolean","SPLIT",FACE,{"disambiguationData":[TD([makeQuery(id+"F1.opExtrude","SWEPT_FACE",FACE,{"disambiguationData":[OSD([subQ2])]})])],"derivedFrom":subQ15})]}),subQ1],"blendedInto":[subQ6,makeQuery(id+"F5.opExtrude","SWEPT_FACE",FACE,{"disambiguationData":[OSD([sQuery(id+"F4.wireOp",EDGE,"E17")])]}),makeQuery(id+"F7.opFillet","BLEND_FACE",FACE,{"disambiguationData":[OSD([subQ5,subQ3,subQ17,subQ0]),TDD([makeQuery(id+"F3.opExtrude","SWEPT_EDGE",EDGE,{"disambiguationData":[OSD([subQ5,subQ3,subQ17,subQ0])]})])]}),makeQuery(id+"F7.opFillet","MERGE",FACE,{"derivedFrom":[makeQuery(id+"F3.boolean.opBoolean","SPLIT",FACE,{"disambiguationData":[TD([makeQuery(id+"F1.opExtrude","SWEPT_FACE",FACE,{"disambiguationData":[OSD([subQ12])]})])],"derivedFrom":subQ15}),makeQuery(id+"F3.boolean.opBoolean","SPLIT",FACE,{"disambiguationData":[TD([makeQuery(id+"F1.opExtrude","SWEPT_FACE",FACE,{"disambiguationData":[OSD([subQ9])]})])],"derivedFrom":subQ15}),makeQuery(id+"F3.boolean.opBoolean","SPLIT",FACE,{"disambiguationData":[TD([makeQuery(id+"F1.opExtrude","SWEPT_FACE",FACE,{"disambiguationData":[OSD([subQ2])]})])],"derivedFrom":subQ15})]}),subQ1]})]});}
            var Q9;
            Q9=makeQuery(id+"F3.opExtrude","CAP_EDGE",EDGE,{"disambiguationData":[OSD([sQuery(id+"F2.wireOp",EDGE,"E15")])],"isStart":true});
            var Q10;
            {var subQ0=sQuery(id+"F2.wireOp",EDGE,"E14");var subQ1=sQuery(id+"F2.wireOp",EDGE,"E13");var subQ2=sQuery(id+"F0.wireOp",EDGE,"E4");var subQ3=sQuery(id+"F0.wireOp",EDGE,"E3");Q10=makeQuery(id+"F10.opFillet","BLEND_EDGE",EDGE,{"blendedFrom":[makeQuery(id+"F1.opExtrude","CAP_EDGE",EDGE,{"disambiguationData":[OSD([subQ2])],"isStart":false}),makeQuery(id+"F7.opFillet","BLEND_FACE",FACE,{"disambiguationData":[OSD([subQ3,subQ2,subQ1,subQ0]),TDD([makeQuery(id+"F3.opExtrude","SWEPT_EDGE",EDGE,{"disambiguationData":[OSD([subQ3,subQ2,subQ1,subQ0])]})])]})],"blendedInto":[makeQuery(id+"F7.opFillet","BLEND_FACE",FACE,{"disambiguationData":[OSD([subQ3,subQ2,subQ1,subQ0]),TDD([makeQuery(id+"F3.opExtrude","SWEPT_EDGE",EDGE,{"disambiguationData":[OSD([subQ3,subQ2,subQ1,subQ0])]})])]})]});}
            var Q11;
            Q11=makeQuery(id+"F3.opExtrude","CAP_EDGE",EDGE,{"disambiguationData":[OSD([sQuery(id+"F2.wireOp",EDGE,"E14")])],"isStart":true});
            var Q12;
            {var subQ0=sQuery(id+"F0.wireOp",EDGE,"E8");var subQ1=sQuery(id+"F0.wireOp",EDGE,"E7");var subQ3=sQuery(id+"F0.wireOp",EDGE,"E6");var subQ5=sQuery(id+"F0.wireOp",EDGE,"E10");var subQ6=sQuery(id+"F0.wireOp",EDGE,"E9");var subQ7=sQuery(id+"F0.wireOp",EDGE,"E5");var subQ8=sQuery(id+"F0.wireOp",EDGE,"E4");var subQ9=sQuery(id+"F0.wireOp",EDGE,"E3");var subQ10=sQuery(id+"F0.wireOp",EDGE,"E2");var subQ11=sQuery(id+"F0.wireOp",EDGE,"E1");var subQ12=sQuery(id+"F0.wireOp",EDGE,"E0");var subQ13=makeQuery(id+"F1.opExtrude","CAP_FACE",FACE,{"disambiguationData":[OSD([subQ12,subQ11,subQ10,subQ9,subQ8,subQ7,subQ3,subQ1,subQ0,subQ6,subQ5,sQuery(id+"F0.wireOp",EDGE,"E11")])],"isStart":false});var subQ15=sQuery(id+"F2.wireOp",EDGE,"E14");var subQ18=makeQuery(id+"F1.opExtrude","SWEPT_FACE",FACE,{"disambiguationData":[OSD([subQ8])]});var subQ20=sQuery(id+"F2.wireOp",EDGE,"E13");var subQ21=makeQuery(id+"F3.opExtrude","SWEPT_FACE",FACE,{"disambiguationData":[OSD([subQ20])]});Q12=makeQuery(id+"F10.opFillet","TWEAK_EDGE",EDGE,{"derivedFrom":[makeQuery(id+"F9.opFillet","BLEND_VERTEX",VERTEX,{"blendedFrom":[makeQuery(id+"F1.opExtrude","CAP_EDGE",EDGE,{"disambiguationData":[OSD([subQ9])],"isStart":false}),subQ18,makeQuery(id+"F5.opExtrude","SWEPT_FACE",FACE,{"disambiguationData":[OSD([sQuery(id+"F4.wireOp",EDGE,"E19")])]}),makeQuery(id+"F7.opFillet","BLEND_FACE",FACE,{"disambiguationData":[OSD([subQ9,subQ8,subQ20,subQ15]),TDD([makeQuery(id+"F3.opExtrude","SWEPT_EDGE",EDGE,{"disambiguationData":[OSD([subQ9,subQ8,subQ20,subQ15])]})])]}),subQ21,makeQuery(id+"F8.opFillet","SPLIT",FACE,{"disambiguationData":[OD(1.0)],"derivedFrom":makeQuery(id+"F7.opFillet","MERGE",FACE,{"derivedFrom":[makeQuery(id+"F3.boolean.opBoolean","SPLIT",FACE,{"disambiguationData":[TD([makeQuery(id+"F1.opExtrude","SWEPT_FACE",FACE,{"disambiguationData":[OSD([subQ10])]})])],"derivedFrom":subQ13}),makeQuery(id+"F3.boolean.opBoolean","SPLIT",FACE,{"disambiguationData":[TD([makeQuery(id+"F1.opExtrude","SWEPT_FACE",FACE,{"disambiguationData":[OSD([subQ7])]})])],"derivedFrom":subQ13}),makeQuery(id+"F3.boolean.opBoolean","SPLIT",FACE,{"disambiguationData":[TD([makeQuery(id+"F1.opExtrude","SWEPT_FACE",FACE,{"disambiguationData":[OSD([subQ0])]})])],"derivedFrom":subQ13})]})})],"blendedInto":[subQ18,makeQuery(id+"F5.opExtrude","SWEPT_FACE",FACE,{"disambiguationData":[OSD([sQuery(id+"F4.wireOp",EDGE,"E19")])]}),makeQuery(id+"F7.opFillet","BLEND_FACE",FACE,{"disambiguationData":[OSD([subQ9,subQ8,subQ20,subQ15]),TDD([makeQuery(id+"F3.opExtrude","SWEPT_EDGE",EDGE,{"disambiguationData":[OSD([subQ9,subQ8,subQ20,subQ15])]})])]}),subQ21,makeQuery(id+"F8.opFillet","SPLIT",FACE,{"disambiguationData":[OD(1.0)],"derivedFrom":makeQuery(id+"F7.opFillet","MERGE",FACE,{"derivedFrom":[makeQuery(id+"F3.boolean.opBoolean","SPLIT",FACE,{"disambiguationData":[TD([makeQuery(id+"F1.opExtrude","SWEPT_FACE",FACE,{"disambiguationData":[OSD([subQ10])]})])],"derivedFrom":subQ13}),makeQuery(id+"F3.boolean.opBoolean","SPLIT",FACE,{"disambiguationData":[TD([makeQuery(id+"F1.opExtrude","SWEPT_FACE",FACE,{"disambiguationData":[OSD([subQ7])]})])],"derivedFrom":subQ13}),makeQuery(id+"F3.boolean.opBoolean","SPLIT",FACE,{"disambiguationData":[TD([makeQuery(id+"F1.opExtrude","SWEPT_FACE",FACE,{"disambiguationData":[OSD([subQ0])]})])],"derivedFrom":subQ13})]})})]})]});}
            var Q13;
            {var subQ0=sQuery(id+"F0.wireOp",EDGE,"E3");Q13=makeQuery(id+"F10.opFillet","BLEND_EDGE",EDGE,{"blendedFrom":[makeQuery(id+"F1.opExtrude","CAP_EDGE",EDGE,{"disambiguationData":[OSD([sQuery(id+"F0.wireOp",EDGE,"E4")])],"isStart":false}),makeQuery(id+"F9.opFillet","BLEND_FACE",FACE,{"disambiguationData":[OSD([subQ0]),TDD([makeQuery(id+"F1.opExtrude","CAP_EDGE",EDGE,{"disambiguationData":[OSD([subQ0])],"isStart":false})])]})],"blendedInto":[makeQuery(id+"F9.opFillet","BLEND_FACE",FACE,{"disambiguationData":[OSD([subQ0]),TDD([makeQuery(id+"F1.opExtrude","CAP_EDGE",EDGE,{"disambiguationData":[OSD([subQ0])],"isStart":false})])]})]});}
            var Q14;
            Q14=makeQuery(id+"F3.opExtrude","CAP_EDGE",EDGE,{"disambiguationData":[OSD([sQuery(id+"F2.wireOp",EDGE,"E13")])],"isStart":true});
            var Q15;
            {var subQ0=sQuery(id+"F2.wireOp",EDGE,"E13");var subQ1=sQuery(id+"F2.wireOp",EDGE,"E12");var subQ2=sQuery(id+"F0.wireOp",EDGE,"E1");var subQ3=sQuery(id+"F0.wireOp",EDGE,"E0");Q15=makeQuery(id+"F9.opFillet","BLEND_EDGE",EDGE,{"blendedFrom":[makeQuery(id+"F1.opExtrude","CAP_EDGE",EDGE,{"disambiguationData":[OSD([subQ2])],"isStart":false}),makeQuery(id+"F7.opFillet","BLEND_FACE",FACE,{"disambiguationData":[OSD([subQ3,subQ2,subQ1,subQ0]),TDD([makeQuery(id+"F3.opExtrude","SWEPT_EDGE",EDGE,{"disambiguationData":[OSD([subQ3,subQ2,subQ1,subQ0])]})])]})],"blendedInto":[makeQuery(id+"F7.opFillet","BLEND_FACE",FACE,{"disambiguationData":[OSD([subQ3,subQ2,subQ1,subQ0]),TDD([makeQuery(id+"F3.opExtrude","SWEPT_EDGE",EDGE,{"disambiguationData":[OSD([subQ3,subQ2,subQ1,subQ0])]})])]})]});}
            var Q16;
            {var subQ0=sQuery(id+"F0.wireOp",EDGE,"E0");Q16=makeQuery(id+"F9.opFillet","BLEND_EDGE",EDGE,{"blendedFrom":[makeQuery(id+"F1.opExtrude","CAP_EDGE",EDGE,{"disambiguationData":[OSD([sQuery(id+"F0.wireOp",EDGE,"E1")])],"isStart":false}),makeQuery(id+"F6.opFillet","BLEND_FACE",FACE,{"disambiguationData":[OSD([subQ0]),TDD([makeQuery(id+"F1.opExtrude","CAP_EDGE",EDGE,{"disambiguationData":[OSD([subQ0])],"isStart":false})])]})],"blendedInto":[makeQuery(id+"F6.opFillet","BLEND_FACE",FACE,{"disambiguationData":[OSD([subQ0]),TDD([makeQuery(id+"F1.opExtrude","CAP_EDGE",EDGE,{"disambiguationData":[OSD([subQ0])],"isStart":false})])]})]});}
            var Q17;
            Q17=makeQuery(id+"F1.opExtrude","SWEPT_EDGE",EDGE,{"disambiguationData":[OSD([sQuery(id+"F0.wireOp",EDGE,"E0"),sQuery(id+"F0.wireOp",EDGE,"E1")])]});
            var Q18;
            {var subQ0=sQuery(id+"F0.wireOp",EDGE,"E1");var subQ1=sQuery(id+"F0.wireOp",EDGE,"E0");Q18=makeQuery(id+"F12.opFillet","TWEAK_EDGE",EDGE,{"derivedFrom":[makeQuery(id+"F9.opFillet","BLEND_VERTEX",VERTEX,{"blendedFrom":[makeQuery(id+"F1.opExtrude","CAP_EDGE",EDGE,{"disambiguationData":[OSD([subQ0])],"isStart":true}),makeQuery(id+"F1.opExtrude","SWEPT_FACE",FACE,{"disambiguationData":[OSD([sQuery(id+"F0.wireOp",EDGE,"E4")])]}),makeQuery(id+"F5.opExtrude","SWEPT_FACE",FACE,{"disambiguationData":[OSD([sQuery(id+"F4.wireOp",EDGE,"E19")])]}),makeQuery(id+"F6.opFillet","BLEND_FACE",FACE,{"disambiguationData":[OSD([subQ1]),TDD([makeQuery(id+"F1.opExtrude","CAP_EDGE",EDGE,{"disambiguationData":[OSD([subQ1])],"isStart":true})])]}),makeQuery(id+"F1.opExtrude","SWEPT_FACE",FACE,{"disambiguationData":[OSD([subQ1])]}),makeQuery(id+"F8.opFillet","SPLIT",FACE,{"disambiguationData":[OD(1.0)],"derivedFrom":makeQuery(id+"F7.opFillet","SPLIT",FACE,{"disambiguationData":[OD(0.0)],"derivedFrom":makeQuery(id+"F6.opFillet","MERGE",FACE,{"derivedFrom":[makeQuery(id+"F1.opExtrude","SWEPT_FACE",FACE,{"disambiguationData":[OSD([subQ0])]}),makeQuery(id+"F1.opExtrude","SWEPT_FACE",FACE,{"disambiguationData":[OSD([sQuery(id+"F0.wireOp",EDGE,"E9")])]}),makeQuery(id+"F3.opExtrude","SWEPT_FACE",FACE,{"disambiguationData":[OSD([sQuery(id+"F2.wireOp",EDGE,"E12")])]}),makeQuery(id+"F5.opExtrude","SWEPT_FACE",FACE,{"disambiguationData":[OSD([sQuery(id+"F4.wireOp",EDGE,"E16")])]})]})})})],"blendedInto":[makeQuery(id+"F1.opExtrude","SWEPT_FACE",FACE,{"disambiguationData":[OSD([sQuery(id+"F0.wireOp",EDGE,"E4")])]}),makeQuery(id+"F5.opExtrude","SWEPT_FACE",FACE,{"disambiguationData":[OSD([sQuery(id+"F4.wireOp",EDGE,"E19")])]}),makeQuery(id+"F6.opFillet","BLEND_FACE",FACE,{"disambiguationData":[OSD([subQ1]),TDD([makeQuery(id+"F1.opExtrude","CAP_EDGE",EDGE,{"disambiguationData":[OSD([subQ1])],"isStart":true})])]}),makeQuery(id+"F1.opExtrude","SWEPT_FACE",FACE,{"disambiguationData":[OSD([subQ1])]}),makeQuery(id+"F8.opFillet","SPLIT",FACE,{"disambiguationData":[OD(1.0)],"derivedFrom":makeQuery(id+"F7.opFillet","SPLIT",FACE,{"disambiguationData":[OD(0.0)],"derivedFrom":makeQuery(id+"F6.opFillet","MERGE",FACE,{"derivedFrom":[makeQuery(id+"F1.opExtrude","SWEPT_FACE",FACE,{"disambiguationData":[OSD([subQ0])]}),makeQuery(id+"F1.opExtrude","SWEPT_FACE",FACE,{"disambiguationData":[OSD([sQuery(id+"F0.wireOp",EDGE,"E9")])]}),makeQuery(id+"F3.opExtrude","SWEPT_FACE",FACE,{"disambiguationData":[OSD([sQuery(id+"F2.wireOp",EDGE,"E12")])]}),makeQuery(id+"F5.opExtrude","SWEPT_FACE",FACE,{"disambiguationData":[OSD([sQuery(id+"F4.wireOp",EDGE,"E16")])]})]})})})]})]});}
            var Q19;
            {var subQ0=sQuery(id+"F0.wireOp",EDGE,"E0");Q19=makeQuery(id+"F12.opFillet","BLEND_EDGE",EDGE,{"blendedFrom":[makeQuery(id+"F5.opExtrude","SWEPT_EDGE",EDGE,{"disambiguationData":[OSD([subQ0,sQuery(id+"F0.wireOp",EDGE,"E1"),sQuery(id+"F4.wireOp",EDGE,"E16"),sQuery(id+"F4.wireOp",EDGE,"E19")])]}),makeQuery(id+"F6.opFillet","BLEND_FACE",FACE,{"disambiguationData":[OSD([subQ0]),TDD([makeQuery(id+"F1.opExtrude","CAP_EDGE",EDGE,{"disambiguationData":[OSD([subQ0])],"isStart":true})])]})],"blendedInto":[makeQuery(id+"F6.opFillet","BLEND_FACE",FACE,{"disambiguationData":[OSD([subQ0]),TDD([makeQuery(id+"F1.opExtrude","CAP_EDGE",EDGE,{"disambiguationData":[OSD([subQ0])],"isStart":true})])]})]});}
            var Q20;
            {var subQ0=sQuery(id+"F0.wireOp",EDGE,"E1");Q20=makeQuery(id+"F12.opFillet","BLEND_EDGE",EDGE,{"blendedFrom":[makeQuery(id+"F5.opExtrude","SWEPT_EDGE",EDGE,{"disambiguationData":[OSD([sQuery(id+"F0.wireOp",EDGE,"E0"),subQ0,sQuery(id+"F4.wireOp",EDGE,"E16"),sQuery(id+"F4.wireOp",EDGE,"E19")])]}),makeQuery(id+"F9.opFillet","BLEND_FACE",FACE,{"disambiguationData":[OSD([subQ0]),TDD([makeQuery(id+"F1.opExtrude","CAP_EDGE",EDGE,{"disambiguationData":[OSD([subQ0])],"isStart":true})])]})],"blendedInto":[makeQuery(id+"F9.opFillet","BLEND_FACE",FACE,{"disambiguationData":[OSD([subQ0]),TDD([makeQuery(id+"F1.opExtrude","CAP_EDGE",EDGE,{"disambiguationData":[OSD([subQ0])],"isStart":true})])]})]});}
            var Q21;
            {var subQ0=sQuery(id+"F0.wireOp",EDGE,"E3");Q21=makeQuery(id+"F11.opFillet","BLEND_EDGE",EDGE,{"blendedFrom":[makeQuery(id+"F5.opExtrude","SWEPT_EDGE",EDGE,{"disambiguationData":[OSD([subQ0,sQuery(id+"F0.wireOp",EDGE,"E4"),sQuery(id+"F4.wireOp",EDGE,"E18"),sQuery(id+"F4.wireOp",EDGE,"E19")])]}),makeQuery(id+"F9.opFillet","BLEND_FACE",FACE,{"disambiguationData":[OSD([subQ0]),TDD([makeQuery(id+"F1.opExtrude","CAP_EDGE",EDGE,{"disambiguationData":[OSD([subQ0])],"isStart":true})])]})],"blendedInto":[makeQuery(id+"F9.opFillet","BLEND_FACE",FACE,{"disambiguationData":[OSD([subQ0]),TDD([makeQuery(id+"F1.opExtrude","CAP_EDGE",EDGE,{"disambiguationData":[OSD([subQ0])],"isStart":true})])]})]});}
            var Q22;
            {var subQ0=sQuery(id+"F0.wireOp",EDGE,"E3");var subQ1=sQuery(id+"F0.wireOp",EDGE,"E4");Q22=makeQuery(id+"F11.opFillet","TWEAK_EDGE",EDGE,{"derivedFrom":[makeQuery(id+"F10.opFillet","BLEND_VERTEX",VERTEX,{"blendedFrom":[makeQuery(id+"F1.opExtrude","CAP_EDGE",EDGE,{"disambiguationData":[OSD([subQ1])],"isStart":true}),makeQuery(id+"F5.opExtrude","SWEPT_FACE",FACE,{"disambiguationData":[OSD([sQuery(id+"F4.wireOp",EDGE,"E18")])]}),makeQuery(id+"F9.opFillet","BLEND_FACE",FACE,{"disambiguationData":[OSD([subQ0]),TDD([makeQuery(id+"F1.opExtrude","CAP_EDGE",EDGE,{"disambiguationData":[OSD([subQ0])],"isStart":true})])]}),makeQuery(id+"F9.opFillet","MERGE",FACE,{"derivedFrom":[makeQuery(id+"F1.opExtrude","SWEPT_FACE",FACE,{"disambiguationData":[OSD([subQ1])]}),makeQuery(id+"F5.opExtrude","SWEPT_FACE",FACE,{"disambiguationData":[OSD([sQuery(id+"F4.wireOp",EDGE,"E19")])]})]}),makeQuery(id+"F1.opExtrude","SWEPT_FACE",FACE,{"disambiguationData":[OSD([subQ0])]})],"blendedInto":[makeQuery(id+"F5.opExtrude","SWEPT_FACE",FACE,{"disambiguationData":[OSD([sQuery(id+"F4.wireOp",EDGE,"E18")])]}),makeQuery(id+"F9.opFillet","BLEND_FACE",FACE,{"disambiguationData":[OSD([subQ0]),TDD([makeQuery(id+"F1.opExtrude","CAP_EDGE",EDGE,{"disambiguationData":[OSD([subQ0])],"isStart":true})])]}),makeQuery(id+"F9.opFillet","MERGE",FACE,{"derivedFrom":[makeQuery(id+"F1.opExtrude","SWEPT_FACE",FACE,{"disambiguationData":[OSD([subQ1])]}),makeQuery(id+"F5.opExtrude","SWEPT_FACE",FACE,{"disambiguationData":[OSD([sQuery(id+"F4.wireOp",EDGE,"E19")])]})]}),makeQuery(id+"F1.opExtrude","SWEPT_FACE",FACE,{"disambiguationData":[OSD([subQ0])]})]})]});}
            var Q23;
            Q23=makeQuery(id+"F1.opExtrude","SWEPT_EDGE",EDGE,{"disambiguationData":[OSD([sQuery(id+"F0.wireOp",EDGE,"E3"),sQuery(id+"F0.wireOp",EDGE,"E4")])]});
            var Q24;
            {var subQ0=sQuery(id+"F0.wireOp",EDGE,"E4");Q24=makeQuery(id+"F11.opFillet","BLEND_EDGE",EDGE,{"blendedFrom":[makeQuery(id+"F5.opExtrude","SWEPT_EDGE",EDGE,{"disambiguationData":[OSD([sQuery(id+"F0.wireOp",EDGE,"E3"),subQ0,sQuery(id+"F4.wireOp",EDGE,"E18"),sQuery(id+"F4.wireOp",EDGE,"E19")])]}),makeQuery(id+"F10.opFillet","BLEND_FACE",FACE,{"disambiguationData":[OSD([subQ0]),TDD([makeQuery(id+"F1.opExtrude","CAP_EDGE",EDGE,{"disambiguationData":[OSD([subQ0])],"isStart":true})])]})],"blendedInto":[makeQuery(id+"F10.opFillet","BLEND_FACE",FACE,{"disambiguationData":[OSD([subQ0]),TDD([makeQuery(id+"F1.opExtrude","CAP_EDGE",EDGE,{"disambiguationData":[OSD([subQ0])],"isStart":true})])]})]});}
            var Q25;
            Q25=makeQuery(id+"F5.opExtrude","CAP_EDGE",EDGE,{"disambiguationData":[OSD([sQuery(id+"F4.wireOp",EDGE,"E18")])],"isStart":true});
            var Q26;
            {var subQ0=sQuery(id+"F0.wireOp",EDGE,"E6");Q26=makeQuery(id+"F12.opFillet","BLEND_EDGE",EDGE,{"blendedFrom":[makeQuery(id+"F5.opExtrude","SWEPT_EDGE",EDGE,{"disambiguationData":[OSD([subQ0,sQuery(id+"F0.wireOp",EDGE,"E7"),sQuery(id+"F4.wireOp",EDGE,"E17"),sQuery(id+"F4.wireOp",EDGE,"E18")])]}),makeQuery(id+"F10.opFillet","BLEND_FACE",FACE,{"disambiguationData":[OSD([subQ0]),TDD([makeQuery(id+"F1.opExtrude","CAP_EDGE",EDGE,{"disambiguationData":[OSD([subQ0])],"isStart":true})])]})],"blendedInto":[makeQuery(id+"F10.opFillet","BLEND_FACE",FACE,{"disambiguationData":[OSD([subQ0]),TDD([makeQuery(id+"F1.opExtrude","CAP_EDGE",EDGE,{"disambiguationData":[OSD([subQ0])],"isStart":true})])]})]});}
            var Q27;
            Q27=makeQuery(id+"F5.opExtrude","CAP_EDGE",EDGE,{"disambiguationData":[OSD([sQuery(id+"F4.wireOp",EDGE,"E16")])],"isStart":true});
            var Q28;
            Q28=makeQuery(id+"F5.opExtrude","CAP_EDGE",EDGE,{"disambiguationData":[OSD([sQuery(id+"F4.wireOp",EDGE,"E19")])],"isStart":true});
            var Q29;
            {var subQ0=sQuery(id+"F0.wireOp",EDGE,"E7");Q29=makeQuery(id+"F12.opFillet","BLEND_EDGE",EDGE,{"blendedFrom":[makeQuery(id+"F5.opExtrude","SWEPT_EDGE",EDGE,{"disambiguationData":[OSD([sQuery(id+"F0.wireOp",EDGE,"E6"),subQ0,sQuery(id+"F4.wireOp",EDGE,"E17"),sQuery(id+"F4.wireOp",EDGE,"E18")])]}),makeQuery(id+"F8.opFillet","BLEND_FACE",FACE,{"disambiguationData":[OSD([subQ0]),TDD([makeQuery(id+"F1.opExtrude","CAP_EDGE",EDGE,{"disambiguationData":[OSD([subQ0])],"isStart":true})])]})],"blendedInto":[makeQuery(id+"F8.opFillet","BLEND_FACE",FACE,{"disambiguationData":[OSD([subQ0]),TDD([makeQuery(id+"F1.opExtrude","CAP_EDGE",EDGE,{"disambiguationData":[OSD([subQ0])],"isStart":true})])]})]});}
            var Q30;
            {var subQ0=sQuery(id+"F0.wireOp",EDGE,"E7");var subQ1=sQuery(id+"F0.wireOp",EDGE,"E6");Q30=makeQuery(id+"F12.opFillet","TWEAK_EDGE",EDGE,{"derivedFrom":[makeQuery(id+"F10.opFillet","BLEND_VERTEX",VERTEX,{"blendedFrom":[makeQuery(id+"F1.opExtrude","CAP_EDGE",EDGE,{"disambiguationData":[OSD([subQ1])],"isStart":true}),makeQuery(id+"F5.opExtrude","SWEPT_FACE",FACE,{"disambiguationData":[OSD([sQuery(id+"F4.wireOp",EDGE,"E18")])]}),makeQuery(id+"F8.opFillet","BLEND_FACE",FACE,{"disambiguationData":[OSD([subQ0]),TDD([makeQuery(id+"F1.opExtrude","CAP_EDGE",EDGE,{"disambiguationData":[OSD([subQ0])],"isStart":true})])]}),makeQuery(id+"F8.opFillet","MERGE",FACE,{"derivedFrom":[makeQuery(id+"F1.opExtrude","SWEPT_FACE",FACE,{"disambiguationData":[OSD([subQ1])]}),makeQuery(id+"F5.opExtrude","SWEPT_FACE",FACE,{"disambiguationData":[OSD([sQuery(id+"F4.wireOp",EDGE,"E17")])]})]}),makeQuery(id+"F1.opExtrude","SWEPT_FACE",FACE,{"disambiguationData":[OSD([subQ0])]})],"blendedInto":[makeQuery(id+"F5.opExtrude","SWEPT_FACE",FACE,{"disambiguationData":[OSD([sQuery(id+"F4.wireOp",EDGE,"E18")])]}),makeQuery(id+"F8.opFillet","BLEND_FACE",FACE,{"disambiguationData":[OSD([subQ0]),TDD([makeQuery(id+"F1.opExtrude","CAP_EDGE",EDGE,{"disambiguationData":[OSD([subQ0])],"isStart":true})])]}),makeQuery(id+"F8.opFillet","MERGE",FACE,{"derivedFrom":[makeQuery(id+"F1.opExtrude","SWEPT_FACE",FACE,{"disambiguationData":[OSD([subQ1])]}),makeQuery(id+"F5.opExtrude","SWEPT_FACE",FACE,{"disambiguationData":[OSD([sQuery(id+"F4.wireOp",EDGE,"E17")])]})]}),makeQuery(id+"F1.opExtrude","SWEPT_FACE",FACE,{"disambiguationData":[OSD([subQ0])]})]})]});}
            var Q31;
            Q31=makeQuery(id+"F1.opExtrude","SWEPT_EDGE",EDGE,{"disambiguationData":[OSD([sQuery(id+"F0.wireOp",EDGE,"E6"),sQuery(id+"F0.wireOp",EDGE,"E7")])]});
            var Q32;
            {var subQ0=sQuery(id+"F0.wireOp",EDGE,"E10");Q32=makeQuery(id+"F12.opFillet","BLEND_EDGE",EDGE,{"blendedFrom":[makeQuery(id+"F5.opExtrude","SWEPT_EDGE",EDGE,{"disambiguationData":[OSD([sQuery(id+"F0.wireOp",EDGE,"E9"),subQ0,sQuery(id+"F4.wireOp",EDGE,"E16"),sQuery(id+"F4.wireOp",EDGE,"E17")])]}),makeQuery(id+"F6.opFillet","BLEND_FACE",FACE,{"disambiguationData":[OSD([subQ0]),TDD([makeQuery(id+"F1.opExtrude","CAP_EDGE",EDGE,{"disambiguationData":[OSD([subQ0])],"isStart":true})])]})],"blendedInto":[makeQuery(id+"F6.opFillet","BLEND_FACE",FACE,{"disambiguationData":[OSD([subQ0]),TDD([makeQuery(id+"F1.opExtrude","CAP_EDGE",EDGE,{"disambiguationData":[OSD([subQ0])],"isStart":true})])]})]});}
            var Q33;
            {var subQ0=sQuery(id+"F0.wireOp",EDGE,"E9");Q33=makeQuery(id+"F12.opFillet","BLEND_EDGE",EDGE,{"blendedFrom":[makeQuery(id+"F5.opExtrude","SWEPT_EDGE",EDGE,{"disambiguationData":[OSD([subQ0,sQuery(id+"F0.wireOp",EDGE,"E10"),sQuery(id+"F4.wireOp",EDGE,"E16"),sQuery(id+"F4.wireOp",EDGE,"E17")])]}),makeQuery(id+"F8.opFillet","BLEND_FACE",FACE,{"disambiguationData":[OSD([subQ0]),TDD([makeQuery(id+"F1.opExtrude","CAP_EDGE",EDGE,{"disambiguationData":[OSD([subQ0])],"isStart":true})])]})],"blendedInto":[makeQuery(id+"F8.opFillet","BLEND_FACE",FACE,{"disambiguationData":[OSD([subQ0]),TDD([makeQuery(id+"F1.opExtrude","CAP_EDGE",EDGE,{"disambiguationData":[OSD([subQ0])],"isStart":true})])]})]});}
            var Q34;
            Q34=makeQuery(id+"F1.opExtrude","SWEPT_EDGE",EDGE,{"disambiguationData":[OSD([sQuery(id+"F0.wireOp",EDGE,"E9"),sQuery(id+"F0.wireOp",EDGE,"E10")])]});
            var Q35;
            {var subQ0=sQuery(id+"F0.wireOp",EDGE,"E9");var subQ1=sQuery(id+"F0.wireOp",EDGE,"E10");Q35=makeQuery(id+"F12.opFillet","TWEAK_EDGE",EDGE,{"derivedFrom":[makeQuery(id+"F8.opFillet","BLEND_VERTEX",VERTEX,{"blendedFrom":[makeQuery(id+"F1.opExtrude","CAP_EDGE",EDGE,{"disambiguationData":[OSD([subQ0])],"isStart":true}),makeQuery(id+"F1.opExtrude","SWEPT_FACE",FACE,{"disambiguationData":[OSD([sQuery(id+"F0.wireOp",EDGE,"E6")])]}),makeQuery(id+"F5.opExtrude","SWEPT_FACE",FACE,{"disambiguationData":[OSD([sQuery(id+"F4.wireOp",EDGE,"E17")])]}),makeQuery(id+"F6.opFillet","BLEND_FACE",FACE,{"disambiguationData":[OSD([subQ1]),TDD([makeQuery(id+"F1.opExtrude","CAP_EDGE",EDGE,{"disambiguationData":[OSD([subQ1])],"isStart":true})])]}),makeQuery(id+"F1.opExtrude","SWEPT_FACE",FACE,{"disambiguationData":[OSD([subQ1])]}),makeQuery(id+"F7.opFillet","SPLIT",FACE,{"disambiguationData":[OD(0.0)],"derivedFrom":makeQuery(id+"F6.opFillet","MERGE",FACE,{"derivedFrom":[makeQuery(id+"F1.opExtrude","SWEPT_FACE",FACE,{"disambiguationData":[OSD([sQuery(id+"F0.wireOp",EDGE,"E1")])]}),makeQuery(id+"F1.opExtrude","SWEPT_FACE",FACE,{"disambiguationData":[OSD([subQ0])]}),makeQuery(id+"F3.opExtrude","SWEPT_FACE",FACE,{"disambiguationData":[OSD([sQuery(id+"F2.wireOp",EDGE,"E12")])]}),makeQuery(id+"F5.opExtrude","SWEPT_FACE",FACE,{"disambiguationData":[OSD([sQuery(id+"F4.wireOp",EDGE,"E16")])]})]})})],"blendedInto":[makeQuery(id+"F1.opExtrude","SWEPT_FACE",FACE,{"disambiguationData":[OSD([sQuery(id+"F0.wireOp",EDGE,"E6")])]}),makeQuery(id+"F5.opExtrude","SWEPT_FACE",FACE,{"disambiguationData":[OSD([sQuery(id+"F4.wireOp",EDGE,"E17")])]}),makeQuery(id+"F6.opFillet","BLEND_FACE",FACE,{"disambiguationData":[OSD([subQ1]),TDD([makeQuery(id+"F1.opExtrude","CAP_EDGE",EDGE,{"disambiguationData":[OSD([subQ1])],"isStart":true})])]}),makeQuery(id+"F1.opExtrude","SWEPT_FACE",FACE,{"disambiguationData":[OSD([subQ1])]}),makeQuery(id+"F7.opFillet","SPLIT",FACE,{"disambiguationData":[OD(0.0)],"derivedFrom":makeQuery(id+"F6.opFillet","MERGE",FACE,{"derivedFrom":[makeQuery(id+"F1.opExtrude","SWEPT_FACE",FACE,{"disambiguationData":[OSD([sQuery(id+"F0.wireOp",EDGE,"E1")])]}),makeQuery(id+"F1.opExtrude","SWEPT_FACE",FACE,{"disambiguationData":[OSD([subQ0])]}),makeQuery(id+"F3.opExtrude","SWEPT_FACE",FACE,{"disambiguationData":[OSD([sQuery(id+"F2.wireOp",EDGE,"E12")])]}),makeQuery(id+"F5.opExtrude","SWEPT_FACE",FACE,{"disambiguationData":[OSD([sQuery(id+"F4.wireOp",EDGE,"E16")])]})]})})]})]});}
            var Q36;
            Q36=makeQuery(id+"F5.opExtrude","CAP_EDGE",EDGE,{"disambiguationData":[OSD([sQuery(id+"F4.wireOp",EDGE,"E17")])],"isStart":true});
            fillet(context, id + "F13", {"entities" : qUnion([Q0, Q1, Q2, Q3, Q4, Q5, Q6, Q7, Q8, Q9, Q10, Q11, Q12, Q13, Q14, Q15, Q16, Q17, Q18, Q19, Q20, Q21, Q22, Q23, Q24, Q25, Q26, Q27, Q28, Q29, Q30, Q31, Q32, Q33, Q34, Q35, Q36]), "radius" : 5.08 * mm, "tangentPropagation" : true, "allowEdgeOverflow" : false});
        }
        {
            var Q0;
            {var subQ0=sQuery(id+"F0.wireOp",EDGE,"E9");var subQ1=sQuery(id+"F0.wireOp",EDGE,"E0");var subQ2=sQuery(id+"F0.wireOp",EDGE,"E1");var subQ3=sQuery(id+"F0.wireOp",EDGE,"E11");var subQ4=sQuery(id+"F0.wireOp",EDGE,"E10");var subQ5=makeQuery(id+"F1.opExtrude","CAP_FACE",FACE,{"disambiguationData":[OSD([subQ1,subQ2,sQuery(id+"F0.wireOp",EDGE,"E2"),sQuery(id+"F0.wireOp",EDGE,"E3"),sQuery(id+"F0.wireOp",EDGE,"E4"),sQuery(id+"F0.wireOp",EDGE,"E5"),sQuery(id+"F0.wireOp",EDGE,"E6"),sQuery(id+"F0.wireOp",EDGE,"E7"),sQuery(id+"F0.wireOp",EDGE,"E8"),subQ0,subQ4,subQ3])],"isStart":false});Q0=makeQuery(id+"F3.boolean.opBoolean","SPLIT",FACE,{"disambiguationData":[TD([makeQuery(id+"F1.opExtrude","SWEPT_FACE",FACE,{"disambiguationData":[OSD([subQ3])]})])],"derivedFrom":subQ5});}
            var sketch = newSketch(context, id + "F14", { "sketchPlane" : qUnion([Q0])});
            skLineSegment(sketch, "E20", {"start": v(-36.63, 34.43) * mm, "end": v(-36.63, 42.05) * mm, "construction": true});
            skLineSegment(sketch, "E21", {"start": v(-37.9, 40.78) * mm, "end": v(-35.36, 40.78) * mm, "construction": true});
            skLineSegment(sketch, "E22", {"start": v(-37.9, 42.05) * mm, "end": v(-37.9, 40.78) * mm, "construction": true});
            skLineSegment(sketch, "E23", {"start": v(-36.63, 40.78) * mm, "end": v(-36.63, 42.05) * mm, "construction": true});
            skCircle(sketch, "E24", {"center": v(-36.63, 41.42) * mm, "radius": 1.27 * mm});
            skPoint(sketch, "E24.centerSnap0", {"position": v(-37.9, 41.42) * mm});
            skSolve(sketch);
        }
        {
            var Q0;
            {var subQ0=sQuery(id+"F14.wireOp",EDGE,"E24");var subQ1=sQuery(id+"F0.wireOp",EDGE,"E9");var subQ2=sQuery(id+"F0.wireOp",EDGE,"E0");var subQ3=sQuery(id+"F0.wireOp",EDGE,"E1");var subQ4=sQuery(id+"F0.wireOp",EDGE,"E11");var subQ5=sQuery(id+"F0.wireOp",EDGE,"E10");var subQ6=makeQuery(id+"F1.opExtrude","CAP_FACE",FACE,{"disambiguationData":[OSD([subQ2,subQ3,sQuery(id+"F0.wireOp",EDGE,"E2"),sQuery(id+"F0.wireOp",EDGE,"E3"),sQuery(id+"F0.wireOp",EDGE,"E4"),sQuery(id+"F0.wireOp",EDGE,"E5"),sQuery(id+"F0.wireOp",EDGE,"E6"),sQuery(id+"F0.wireOp",EDGE,"E7"),sQuery(id+"F0.wireOp",EDGE,"E8"),subQ1,subQ5,subQ4])],"isStart":false});var subQ7=makeQuery(id+"F3.boolean.opBoolean","SPLIT",FACE,{"disambiguationData":[TD([makeQuery(id+"F1.opExtrude","SWEPT_FACE",FACE,{"disambiguationData":[OSD([subQ4])]})])],"derivedFrom":subQ6});var subQ8=makeQuery(id+"F14.imprint","INTERSECT",VERTEX,{"derivedFrom":[makeQuery(id+"F6.opFillet","BLEND_EDGE",EDGE,{"blendedFrom":[makeQuery(id+"F1.opExtrude","CAP_EDGE",EDGE,{"disambiguationData":[OSD([subQ2])],"isStart":false}),subQ7],"blendedInto":[subQ7]}),subQ0]});Q0=makeQuery(id+"F14.imprint","IMPRINT",FACE,{"disambiguationData":[TD([[makeQuery(id+"F14.imprint","IMPRINT",EDGE,{"disambiguationData":[TD([[subQ8,-1.0]])],"derivedFrom":subQ0}),1.0]])]});}
            var Q1;
            {var subQ0=sQuery(id+"F14.wireOp",EDGE,"E24");var subQ1=sQuery(id+"F0.wireOp",EDGE,"E9");var subQ2=sQuery(id+"F0.wireOp",EDGE,"E0");var subQ3=sQuery(id+"F0.wireOp",EDGE,"E1");var subQ4=sQuery(id+"F0.wireOp",EDGE,"E11");var subQ5=sQuery(id+"F0.wireOp",EDGE,"E10");var subQ6=makeQuery(id+"F1.opExtrude","CAP_FACE",FACE,{"disambiguationData":[OSD([subQ2,subQ3,sQuery(id+"F0.wireOp",EDGE,"E2"),sQuery(id+"F0.wireOp",EDGE,"E3"),sQuery(id+"F0.wireOp",EDGE,"E4"),sQuery(id+"F0.wireOp",EDGE,"E5"),sQuery(id+"F0.wireOp",EDGE,"E6"),sQuery(id+"F0.wireOp",EDGE,"E7"),sQuery(id+"F0.wireOp",EDGE,"E8"),subQ1,subQ5,subQ4])],"isStart":false});var subQ7=makeQuery(id+"F6.opFillet","BLEND_EDGE",EDGE,{"blendedFrom":[makeQuery(id+"F1.opExtrude","CAP_EDGE",EDGE,{"disambiguationData":[OSD([subQ4])],"isStart":false}),makeQuery(id+"F3.boolean.opBoolean","SPLIT",FACE,{"disambiguationData":[TD([makeQuery(id+"F1.opExtrude","SWEPT_FACE",FACE,{"disambiguationData":[OSD([subQ4])]})])],"derivedFrom":subQ6})],"blendedInto":[makeQuery(id+"F3.boolean.opBoolean","SPLIT",FACE,{"disambiguationData":[TD([makeQuery(id+"F1.opExtrude","SWEPT_FACE",FACE,{"disambiguationData":[OSD([subQ4])]})])],"derivedFrom":subQ6})]});var subQ8=makeQuery(id+"F14.imprint","INTERSECT",VERTEX,{"disambiguationData":[OD(0.0)],"derivedFrom":[subQ7,subQ0]});Q1=makeQuery(id+"F14.imprint","IMPRINT",FACE,{"disambiguationData":[TD([[makeQuery(id+"F14.imprint","IMPRINT",EDGE,{"disambiguationData":[TD([[subQ8,-1.0]])],"derivedFrom":subQ0}),1.0]])]});}
            var Q2;
            Q2=sQuery(id+"F14.wireOp",EDGE,"E24");
            extrude(context, id + "F15", {"entities" : qUnion([Q0, Q1]), "operationType" : NewBodyOperationType.REMOVE, "surfaceEntities" : qUnion([Q2]), "oppositeDirection" : true, "depth" : 12.7 * mm});
        }
    });
